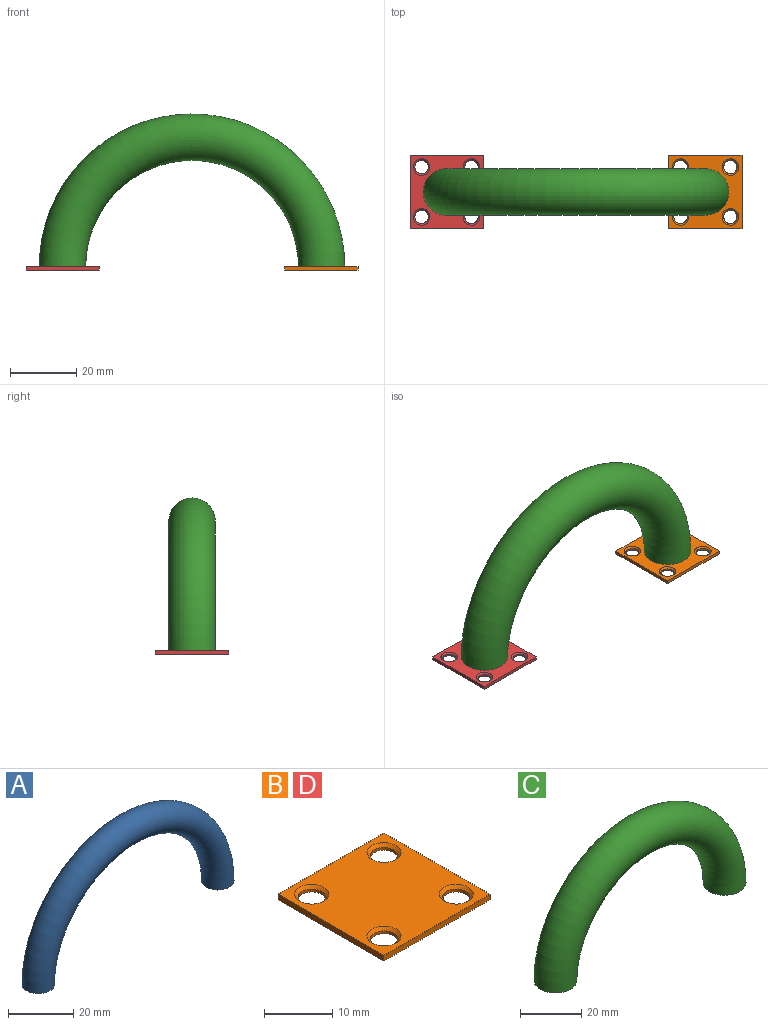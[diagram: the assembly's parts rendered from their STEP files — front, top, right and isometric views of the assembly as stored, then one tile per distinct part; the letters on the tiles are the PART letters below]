
ASSEMBLY  parts=4 mates=3
PART A: 3 faces, bbox 95.3x10x47.6 mm
  f0: plane 10x10mm, normal (0,0,-1), area 78.5mm2, adj f2
  f1: plane 10x10mm, normal (0,0,-1), area 78.5mm2, adj f2
  f2: torus R=39mm, axis (0,-1,0), area 3849.1mm2, adj f0,f1
PART B: 14 faces, bbox 22x22x1 mm
  f0: plane 22x1mm, normal (0,-1,0), area 22mm2, adj f1,f7,f8,f9
  f1: plane 22x1mm, normal (1,0,0), area 22mm2, adj f0,f2,f8,f9
  f2: plane 22x1mm, normal (0,1,0), area 22mm2, adj f1,f7,f8,f9
  f3: cylinder r=2mm len=4mm, axis (0,0,-1), area 6.3mm2, adj f9,f13
  f4: cylinder r=2mm len=4mm, axis (0,0,-1), area 6.3mm2, adj f9,f10
  f5: cylinder r=2mm len=4mm, axis (0,0,-1), area 6.3mm2, adj f9,f11
  f6: cylinder r=2mm len=4mm, axis (0,0,-1), area 6.3mm2, adj f9,f12
  f7: plane 22x1mm, normal (-1,0,0), area 22mm2, adj f0,f2,f8,f9
  f8: plane 22x22mm, normal (0,0,1), area 405.5mm2, adj f0,f1,f2,f7,f10,f11,f12,f13
  f9: plane 22x22mm, normal (0,0,-1), area 433.7mm2, adj f0,f1,f2,f3,f4,f5,f6,f7
  f10: cone r=2mm half-angle=45deg, axis (0,0,1), area 10mm2, adj f4,f8
  f11: cone r=2mm half-angle=45deg, axis (0,0,1), area 10mm2, adj f5,f8
  f12: cone r=2mm half-angle=45deg, axis (0,0,1), area 10mm2, adj f6,f8
  f13: cone r=2mm half-angle=45deg, axis (0,0,1), area 10mm2, adj f3,f8
PART C: 4 faces, bbox 99.6x14x49.8 mm
  f0: plane 14x14mm, normal (0,0,-1), area 40.8mm2, adj f2,f3
  f1: plane 14x14mm, normal (0,0,-1), area 40.8mm2, adj f2,f3
  f2: torus R=39mm, axis (0,-1,0), area 5388.8mm2, adj f0,f1
  f3: torus R=39mm, axis (0,-1,0), area 4619mm2, adj f0,f1
PART D: same geometry as B
PLACE A t=(-28.18,-7.14,-10.55)mm
PLACE B t=(10.82,-12.14,-11.55)mm
PLACE C t=(-28.18,-5.14,-10.55)mm
PLACE D t=(-67.18,-12.14,-11.55)mm
MATE revolute A.f2 <-> C.f2  axis (0,-1,0) through (-28.18,-12.14,-10.55)mm
MATE fastened B.f8 <-> C.f1  axis (0,0,1) through (10.82,-12.14,-10.55)mm
MATE fastened D.f8 <-> A.f0  axis (0,0,1) through (-67.18,-12.14,-10.55)mm
